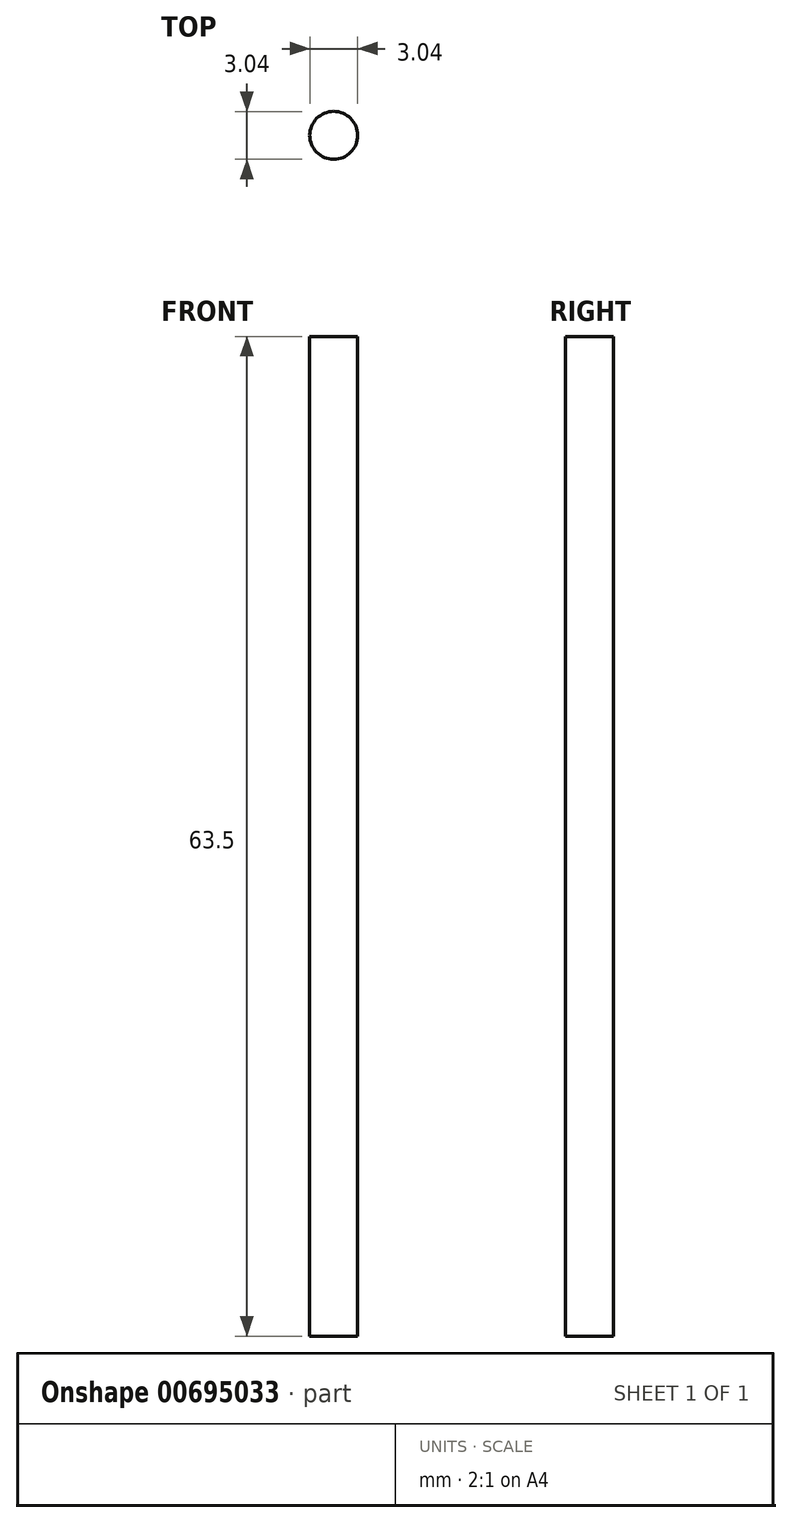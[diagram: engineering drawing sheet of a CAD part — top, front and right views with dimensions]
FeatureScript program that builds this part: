
annotation { "Feature Type Name" : "Feature", "Feature Type Description" : "" }
export const myFeature = defineFeature(function(context is Context, id is Id, definition is map)
    precondition{}
    {
        {
            var Q0;
            Q0=qCreatedBy(makeId("Top.planeOp"),FACE);
            var sketch = newSketch(context, id + "F0", { "sketchPlane" : qUnion([Q0])});
            skCircle(sketch, "E0", {"center": v(0, 0) * mm, "radius": 1.52 * mm});
            skLineSegment(sketch, "E1", {"start": v(0, 0) * mm, "end": v(0, 1.52) * mm});
            skSolve(sketch);
        }
        {
            var Q0;
            Q0 = qSketchRegion(id + "F0", true);
            extrude(context, id + "F1", {"entities" : qUnion([Q0]), "depth" : 63.5 * mm, "offsetDistance" : 25.4 * mm});
        }
    });
